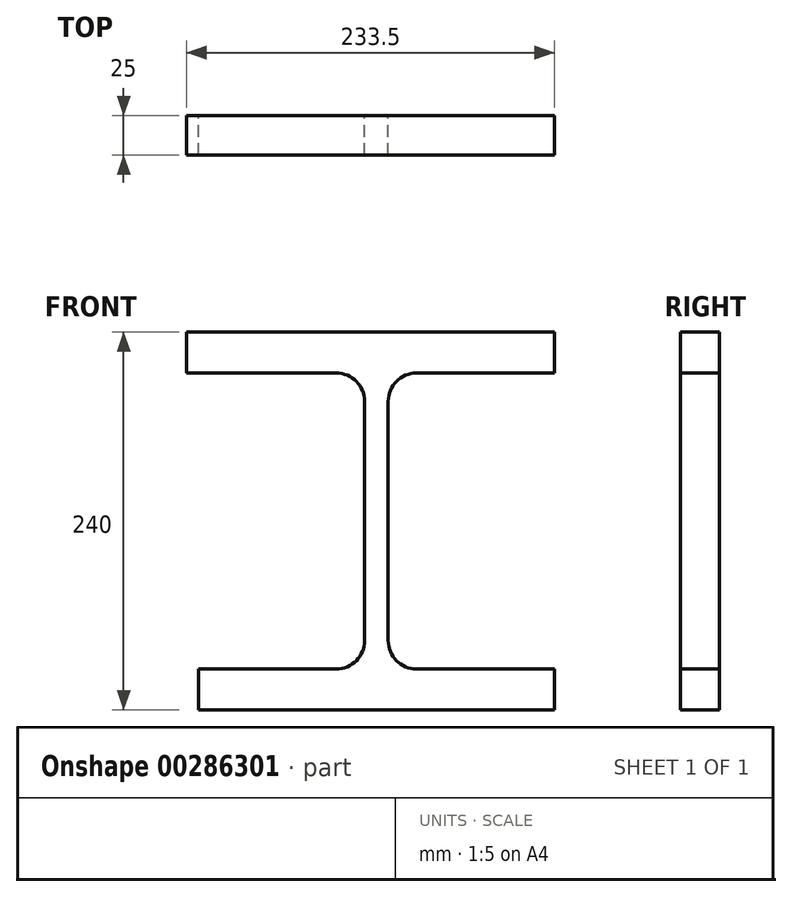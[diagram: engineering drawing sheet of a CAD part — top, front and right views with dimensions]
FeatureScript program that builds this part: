
annotation { "Feature Type Name" : "Feature", "Feature Type Description" : "" }
export const myFeature = defineFeature(function(context is Context, id is Id, definition is map)
    precondition{}
    {
        {
            var Q0;
            Q0=qCreatedBy(makeId("Front.planeOp"),FACE);
            var sketch = newSketch(context, id + "F0", { "sketchPlane" : qUnion([Q0])});
            skLineSegment(sketch, "E0", {"start": v(-60.63, -37.74) * mm, "end": v(165.37, -37.74) * mm});
            skLineSegment(sketch, "E1", {"start": v(165.37, -37.74) * mm, "end": v(165.37, -11.74) * mm});
            skLineSegment(sketch, "E2", {"start": v(-60.63, -37.74) * mm, "end": v(-60.63, -11.74) * mm});
            skLineSegment(sketch, "E3", {"start": v(-60.63, -11.74) * mm, "end": v(26.87, -11.74) * mm});
            skLineSegment(sketch, "E4", {"start": v(77.87, -11.74) * mm, "end": v(165.37, -11.74) * mm});
            skLineSegment(sketch, "E5", {"start": v(44.87, 6.26) * mm, "end": v(44.87, 158.26) * mm});
            skLineSegment(sketch, "E6", {"start": v(52.37, 176.26) * mm, "end": v(59.87, 176.26) * mm});
            skLineSegment(sketch, "E7", {"start": v(59.87, 158.26) * mm, "end": v(59.87, 6.26) * mm});
            skLineSegment(sketch, "E8", {"start": v(77.87, 176.26) * mm, "end": v(165.37, 176.26) * mm});
            skLineSegment(sketch, "E9", {"start": v(26.87, 176.26) * mm, "end": v(-68.13, 176.26) * mm});
            skLineSegment(sketch, "E10", {"start": v(-68.13, 176.26) * mm, "end": v(-68.13, 202.26) * mm});
            skLineSegment(sketch, "E11", {"start": v(165.37, 176.26) * mm, "end": v(165.37, 202.26) * mm});
            skLineSegment(sketch, "E12", {"start": v(165.37, 202.26) * mm, "end": v(-68.13, 202.26) * mm});
            skPoint(sketch, "E13.visualSharp", {"position": v(59.87, 176.26) * mm});
            skArc(sketch, "E13.filletArc", {"start": v(64.87, 176.26) * mm, "mid": v(61.34, 174.8) * mm, "end": v(59.87, 171.26) * mm});
            skArc(sketch, "E14.filletArc", {"start": v(77.87, 176.26) * mm, "mid": v(65.14, 170.99) * mm, "end": v(59.87, 158.26) * mm});
            skPoint(sketch, "E15.visualSharp", {"position": v(44.87, 176.26) * mm});
            skArc(sketch, "E15.filletArc", {"start": v(44.87, 158.26) * mm, "mid": v(39.6, 170.99) * mm, "end": v(26.87, 176.26) * mm});
            skArc(sketch, "E16.filletArc", {"start": v(59.87, 6.26) * mm, "mid": v(65.14, -6.47) * mm, "end": v(77.87, -11.74) * mm});
            skPoint(sketch, "E17.newPointA", {"position": v(44.87, -11.74) * mm});
            skPoint(sketch, "E17.newPointB", {"position": v(52.37, -11.74) * mm});
            skArc(sketch, "E17.filletArc", {"start": v(26.87, -11.74) * mm, "mid": v(39.6, -6.47) * mm, "end": v(44.87, 6.26) * mm});
            skSolve(sketch);
        }
        {
            var Q0;
            Q0 = qSketchRegion(id + "F0", true);
            extrude(context, id + "F1", {"entities" : qUnion([Q0]), "depth" : 25 * mm});
        }
    });
